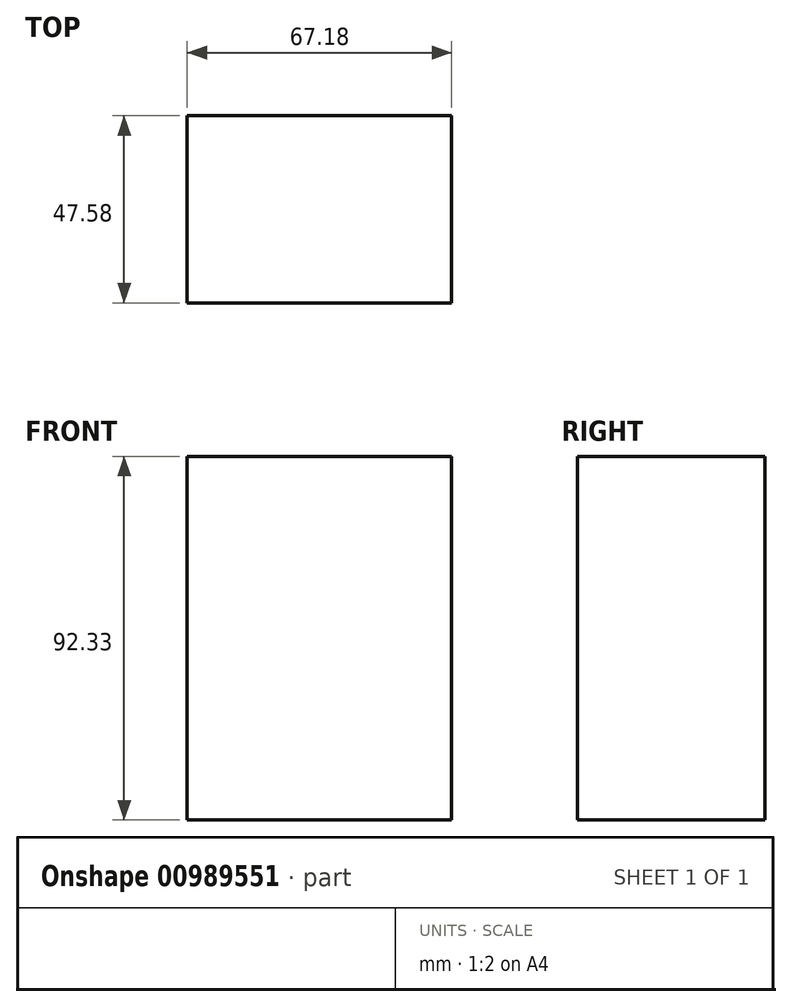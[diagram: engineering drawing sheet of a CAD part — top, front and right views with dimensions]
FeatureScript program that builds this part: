
annotation { "Feature Type Name" : "Feature", "Feature Type Description" : "" }
export const myFeature = defineFeature(function(context is Context, id is Id, definition is map)
    precondition{}
    {
        {
            var Q0;
            Q0=qCreatedBy(makeId("Front.planeOp"),FACE);
            var sketch = newSketch(context, id + "F0", { "sketchPlane" : qUnion([Q0])});
            skLineSegment(sketch, "E0.bottom", {"start": v(-29.79, 50.03) * mm, "end": v(37.39, 50.03) * mm});
            skLineSegment(sketch, "E0.top", {"start": v(-29.79, -42.3) * mm, "end": v(37.39, -42.3) * mm});
            skLineSegment(sketch, "E0.left", {"start": v(-29.79, 50.03) * mm, "end": v(-29.79, -42.3) * mm});
            skLineSegment(sketch, "E0.right", {"start": v(37.39, 50.03) * mm, "end": v(37.39, -42.3) * mm});
            skSolve(sketch);
        }
        {
            var Q0;
            Q0=makeQuery(id+"F0.imprint","IMPRINT",FACE,{"disambiguationData":[TD([[makeQuery(id+"F0.imprint","IMPRINT",EDGE,{"derivedFrom":sQuery(id+"F0.wireOp",EDGE,"E0.bottom")}),-1.0]])]});
            extrude(context, id + "F1", {"entities" : qUnion([Q0]), "depth" : 47.58 * mm, "offsetDistance" : 25.4 * mm});
        }
    });
